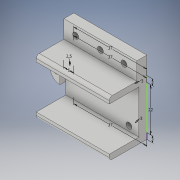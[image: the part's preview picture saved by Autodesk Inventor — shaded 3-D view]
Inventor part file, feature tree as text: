
AUTODESK INVENTOR PART (.ipt)
format: ipt  version: 2019 (Build 230136000, 136)  size: 171,520 bytes
history: native  units: mm
features: extrude x6, sketch x4, fillet x2, other x1, projected_geometry x1
ambient origin geometry x8: Origin, YZ Plane, XZ Plane, XY Plane, X Axis, Y Axis, Z Axis, Center Point
bodies: Body1 (feature_tree)
feature tree (14):
  other  "Bryła1"
  sketch  "Szkic1"
  extrude  "Wyciągnięcie proste1"  Depth=37.0mm
  extrude  "Wyciągnięcie proste2"  Depth=22.0mm
  extrude  "Wyciągnięcie proste3"  Depth=5.0mm
  extrude  "Wyciągnięcie proste4"  Depth=2.5mm
  fillet  "Zaokrąglenie2"  Radius=3.0mm
  fillet  "Zaokrąglenie3"  Radius=3.0mm
  extrude  "Wyciągnięcie proste5"  Depth=37.0mm
  extrude  "Wyciągnięcie proste6"  Depth=3.0mm
  sketch  "Szkic2"
  sketch  "Szkic3"
  projected_geometry  "Pętla rzutowana1"
  sketch  "Szkic4"
